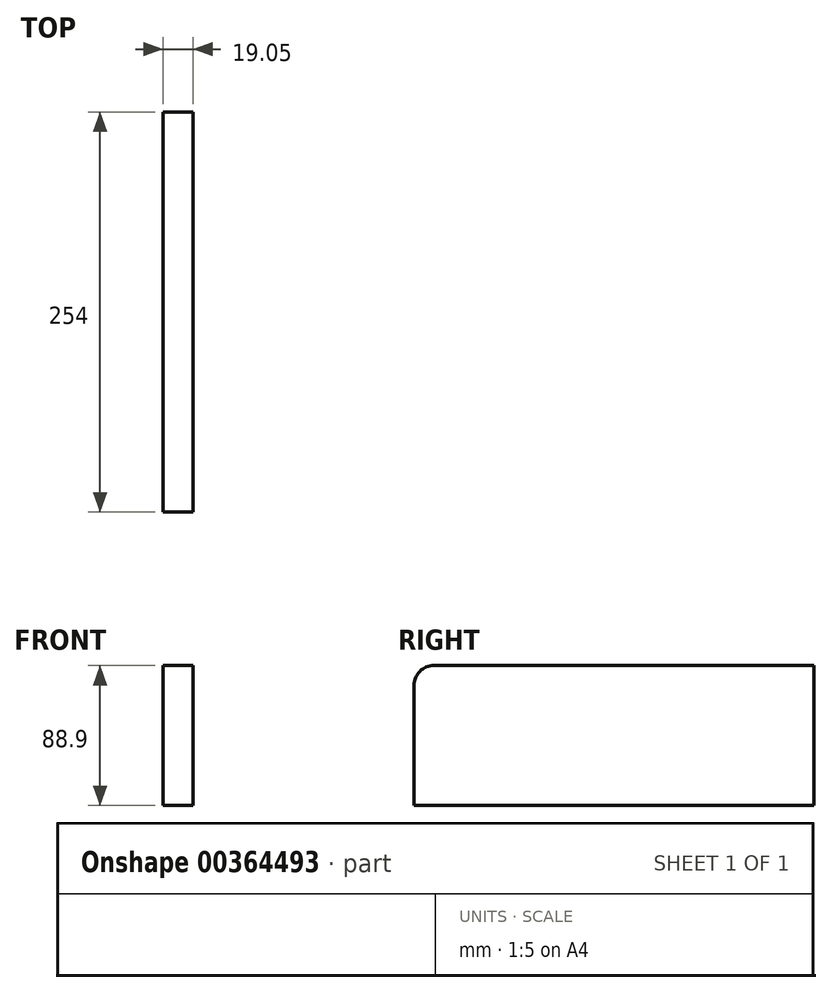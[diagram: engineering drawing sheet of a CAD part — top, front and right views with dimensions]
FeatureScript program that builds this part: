
annotation { "Feature Type Name" : "Feature", "Feature Type Description" : "" }
export const myFeature = defineFeature(function(context is Context, id is Id, definition is map)
    precondition{}
    {
        {
            var Q0;
            Q0=qCreatedBy(makeId("Right.planeOp"),FACE);
            var sketch = newSketch(context, id + "F0", { "sketchPlane" : qUnion([Q0])});
            skLineSegment(sketch, "E0.bottom", {"start": v(0, 0) * mm, "end": v(254, 0) * mm});
            skLineSegment(sketch, "E0.top", {"start": v(12.7, 88.9) * mm, "end": v(254, 88.9) * mm});
            skLineSegment(sketch, "E0.left", {"start": v(0, 0) * mm, "end": v(0, 76.2) * mm});
            skLineSegment(sketch, "E0.right", {"start": v(254, 0) * mm, "end": v(254, 88.9) * mm});
            skPoint(sketch, "E1.visualSharp", {"position": v(0, 88.9) * mm});
            skArc(sketch, "E1.filletArc", {"start": v(12.7, 88.9) * mm, "mid": v(3.72, 85.18) * mm, "end": v(0, 76.2) * mm});
            skSolve(sketch);
        }
        {
            var Q0;
            Q0=makeQuery(id+"F0.imprint","IMPRINT",FACE,{"disambiguationData":[TD([[makeQuery(id+"F0.imprint","IMPRINT",EDGE,{"derivedFrom":sQuery(id+"F0.wireOp",EDGE,"E0.bottom")}),1.0]])]});
            extrude(context, id + "F1", {"entities" : qUnion([Q0]), "depth" : 19.05 * mm});
        }
    });
